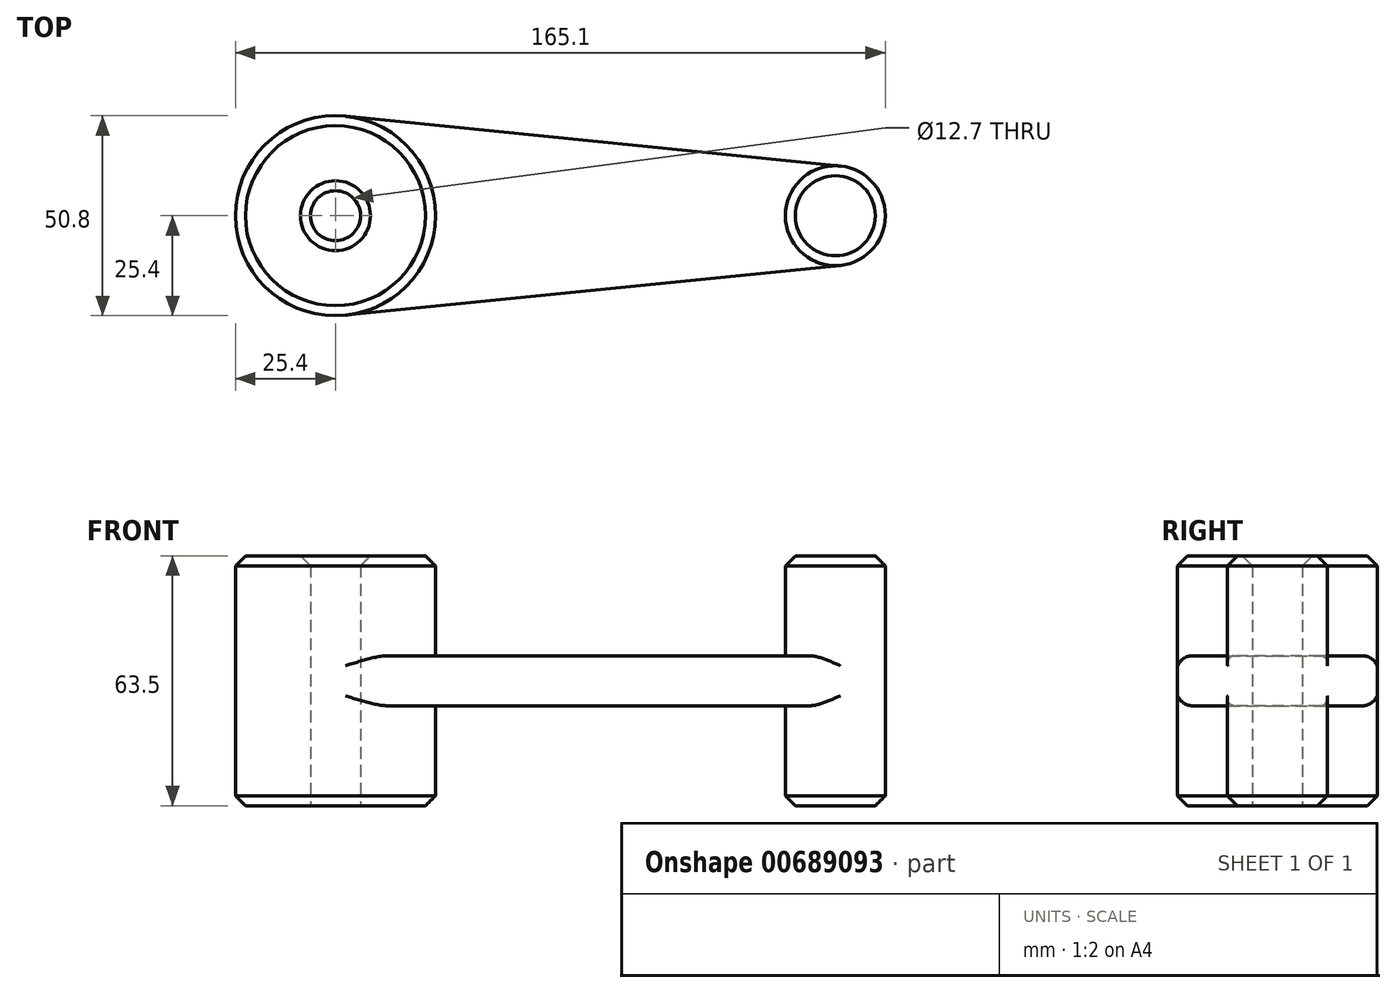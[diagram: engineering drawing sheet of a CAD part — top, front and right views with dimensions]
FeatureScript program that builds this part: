
annotation { "Feature Type Name" : "Feature", "Feature Type Description" : "" }
export const myFeature = defineFeature(function(context is Context, id is Id, definition is map)
    precondition{}
    {
        {
            var Q0;
            Q0=qCreatedBy(makeId("Top.planeOp"),FACE);
            var sketch = newSketch(context, id + "F0", { "sketchPlane" : qUnion([Q0])});
            skCircle(sketch, "E0", {"center": v(0, 0) * mm, "radius": 25.4 * mm});
            skCircle(sketch, "E1", {"center": v(127, 0) * mm, "radius": 12.7 * mm});
            skLineSegment(sketch, "E2", {"start": v(2.54, -25.27) * mm, "end": v(128.27, -12.64) * mm});
            skLineSegment(sketch, "E3", {"start": v(2.54, 25.27) * mm, "end": v(128.27, 12.64) * mm});
            skCircle(sketch, "E4", {"center": v(0, 0) * mm, "radius": 6.35 * mm});
            skSolve(sketch);
        }
        {
            var Q0;
            Q0=makeQuery(id+"F0.imprint","IMPRINT",FACE,{"disambiguationData":[TD([[makeQuery(id+"F0.imprint","IMPRINT",EDGE,{"derivedFrom":sQuery(id+"F0.wireOp",EDGE,"E4")}),-1.0]])]});
            extrude(context, id + "F1", {"entities" : qUnion([Q0]), "depth" : 38.1 * mm, "offsetDistance" : 25.4 * mm, "hasSecondDirection" : true, "secondDirectionOppositeDirection" : true, "secondDirectionDepth" : 25.4 * mm});
        }
        {
            var Q0;
            {var subQ0=sQuery(id+"F0.wireOp",EDGE,"E2");Q0=makeQuery(id+"F0.imprint","IMPRINT",FACE,{"disambiguationData":[TD([[makeQuery(id+"F0.imprint","IMPRINT",EDGE,{"derivedFrom":subQ0}),1.0]])]});}
            extrude(context, id + "F2", {"entities" : qUnion([Q0]), "operationType" : NewBodyOperationType.ADD, "depth" : 12.7 * mm, "offsetDistance" : 25.4 * mm});
        }
        {
            var Q0;
            {var subQ0=sQuery(id+"F0.wireOp",EDGE,"E1");var subQ1=makeQuery(id+"F0.imprint","INTERSECT",VERTEX,{"derivedFrom":[subQ0,sQuery(id+"F0.wireOp",EDGE,"E2")]});Q0=makeQuery(id+"F0.imprint","IMPRINT",FACE,{"disambiguationData":[TD([[makeQuery(id+"F0.imprint","IMPRINT",EDGE,{"disambiguationData":[TD([[subQ1,1.0]])],"derivedFrom":subQ0}),1.0]])]});}
            var Q1;
            Q1=sQuery(id+"F0.wireOp",EDGE,"E1");
            extrude(context, id + "F3", {"entities" : qUnion([Q0]), "operationType" : NewBodyOperationType.ADD, "surfaceEntities" : qUnion([Q1]), "oppositeDirection" : true, "depth" : 25.4 * mm, "offsetDistance" : 25.4 * mm, "hasSecondDirection" : true, "secondDirectionOppositeDirection" : false, "secondDirectionDepth" : 38.1 * mm});
        }
        {
            var Q0;
            Q0=makeQuery(id+"F1.opExtrude","CAP_FACE",FACE,{"disambiguationData":[OSD([sQuery(id+"F0.wireOp",EDGE,"E0"),sQuery(id+"F0.wireOp",EDGE,"E4")])],"isStart":false});
            var Q1;
            Q1=makeQuery(id+"F1.opExtrude","CAP_EDGE",EDGE,{"disambiguationData":[OSD([sQuery(id+"F0.wireOp",EDGE,"E0")])],"isStart":true});
            var Q2;
            Q2=makeQuery(id+"F3.opExtrude","CAP_EDGE",EDGE,{"disambiguationData":[OSD([sQuery(id+"F0.wireOp",EDGE,"E1")])],"isStart":false});
            var Q3;
            Q3=makeQuery(id+"F3.opExtrude","CAP_EDGE",EDGE,{"disambiguationData":[OSD([sQuery(id+"F0.wireOp",EDGE,"E1")])],"isStart":true});
            chamfer(context, id + "F4", {"entities" : qUnion([Q0, Q1, Q2, Q3]), "width" : 2.54 * mm, "tangentPropagation" : true});
        }
        {
            var Q0;
            Q0=makeQuery(id+"F2.opExtrude","CAP_EDGE",EDGE,{"disambiguationData":[OSD([sQuery(id+"F0.wireOp",EDGE,"E2")])],"isStart":true});
            var Q1;
            Q1=makeQuery(id+"F2.opExtrude","CAP_EDGE",EDGE,{"disambiguationData":[OSD([sQuery(id+"F0.wireOp",EDGE,"E2")])],"isStart":false});
            var Q2;
            Q2=makeQuery(id+"F2.opExtrude","CAP_EDGE",EDGE,{"disambiguationData":[OSD([sQuery(id+"F0.wireOp",EDGE,"E3")])],"isStart":true});
            var Q3;
            Q3=makeQuery(id+"F2.opExtrude","CAP_EDGE",EDGE,{"disambiguationData":[OSD([sQuery(id+"F0.wireOp",EDGE,"E3")])],"isStart":false});
            fillet(context, id + "F5", {"entities" : qUnion([Q0, Q1, Q2, Q3]), "radius" : 2.54 * mm, "tangentPropagation" : true, "allowEdgeOverflow" : false});
        }
    });
